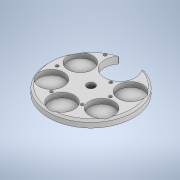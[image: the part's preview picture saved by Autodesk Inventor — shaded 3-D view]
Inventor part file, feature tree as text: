
AUTODESK INVENTOR PART (.ipt)
format: ipt  version: 2021 (Build 250183000, 183)  size: 220,160 bytes
history: native  units: mm
features: extrude x4, sketch x4, chamfer x2
ambient origin geometry x8: Origin, YZ Plane, XZ Plane, XY Plane, X Axis, Y Axis, Z Axis, Center Point
bodies: Solid1 (feature_tree)
feature tree (10):
  extrude  "Extrusion1"  Depth=8.2mm
  extrude  "Extrusion2"  Depth=30.0mm
  chamfer  "Chamfer1"  Distance=7.0mm
  chamfer  "Chamfer2"  Distance=25.4mm
  extrude  "Extrusion3"  Depth=5.0mm TaperAngle=0.0deg
  extrude  "Extrusion4"  Depth=2.0mm TaperAngle=45.0deg
  sketch  "Sketch1"  dims[d0=88.0mm d1=8.2mm]
  sketch  "Sketch2"  dims[d2=25.4mm d3=30.0mm]
  sketch  "Sketch3"  dims[d4=32.0mm]
  sketch  "Sketch4"  dims[d5=25.4mm d6=7.0mm d7=0.0mm d8=25.4mm d9=5.0mm d10=0.0mm d11=2.0mm d12=2.0mm d13=45.0deg d14=4.0mm d15=2.0mm d16=45.0deg d17=3.5mm d18=2.7mm d19=0.0mm d20=0.0mm d28=80.0mm d29=70.0mm d30=60.0mm d31=50.0mm d32=40.0mm d38=30.0mm d45=3.0mm d46=60.0deg d47=60.0deg d48=60.0deg d49=60.0deg d50=0.0mm d51=0.0mm]
